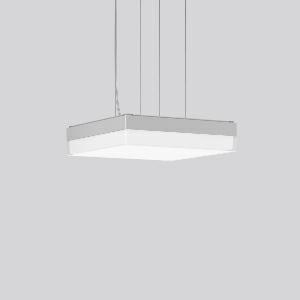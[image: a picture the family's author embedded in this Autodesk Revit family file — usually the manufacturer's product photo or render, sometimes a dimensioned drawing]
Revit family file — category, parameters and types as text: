
# Revit family: flat_slim_square_312542_004_730_de0b
name_source: partatom
category: Lighting Fixtures
units: mm (PartAtom-declared; Revit-internal decimal feet)

## family parameters
Cut with Voids When Loaded = No
Host = Face
Light Source = No
Part Type = Normal
Room Calculation Point = No
Round Connector Dimension = Use Diameter
Shared = No

## types (1)
- MultiLumen 2 840 (1 x LED Modul 840, 2300 lm, 4000)
    Apparent Load = 21 VA
    CIE Flux Codes = 43 75 93 91 100
    Color Rendering = 80
    Color Temperature = 4000
    Default Elevation = 1800 mm
    Height = 70 mm
    Lamp = 1 x LED Modul 840
    Lamp Light Flux = 2300 lm
    Lamp count = 1
    Length = 300 mm
    Lifetime = 50000 h
    Luminous efficacy = 110 lm/W
    Manufacturer = RZB
    ModVariant = No
    Model = 312542.004.730
    Mounting Place = Ceiling
    Mounting Type = Pendant
    Number of Poles = 1
    OnlyDefault = Yes
    Power Factor = 1
    Product Name = FLAT SLIM square
    Product group = Pendant luminaires
    ProductGroupID = 902
    Protection Class = Protection class I
    Protection Degree = IP 40
    RLX_Detail_Level = 1
    RLX_Emergency_Light_Flux = 0 lm
    RLX_Emergency_Type = 0
    RLX_Emergency_Type_DB = No
    RlxData = <blob elided: 14533 chars, md5=8943d5a3>
    Socket = socket
    Standby Power = 0 W
    System Light Flux = 2300 lm
    System Power = 21 W
    Type Comments = MultiLumen 2 840
    Type Image = 312542.004.jpg
    URL = http://relux.com
    VarID = multilumen_2_840
    Voltage = 230 V
    Voltage Range = 220-240 V
    Weight = 0.00 kg
    Width = 300 mm

## geometry (parser evidence)
native form markers: Sweep x12
no freeform markers — native parametric forms only
